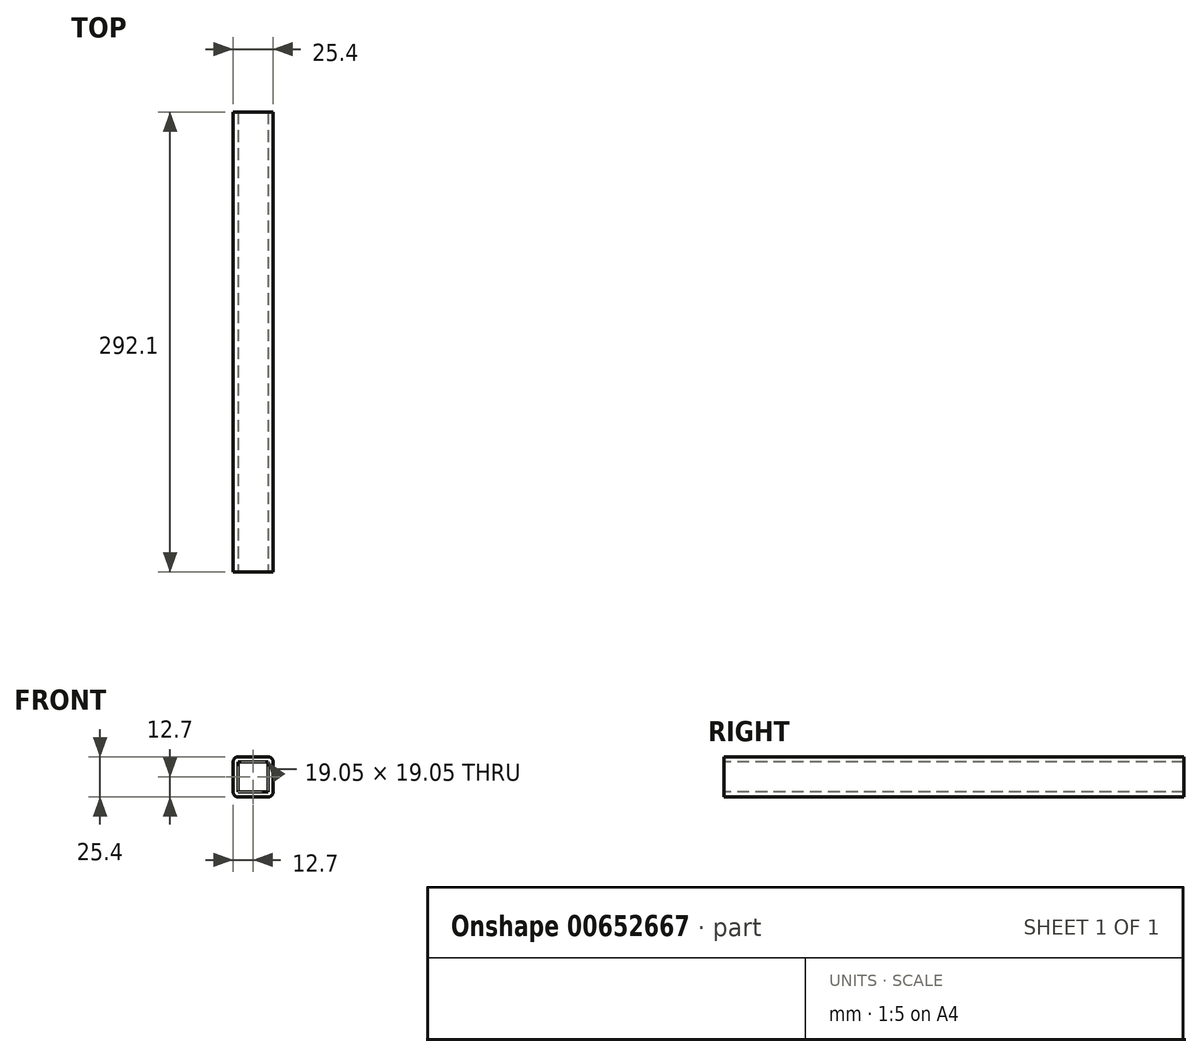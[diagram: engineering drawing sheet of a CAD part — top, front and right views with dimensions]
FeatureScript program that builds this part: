
annotation { "Feature Type Name" : "Feature", "Feature Type Description" : "" }
export const myFeature = defineFeature(function(context is Context, id is Id, definition is map)
    precondition{}
    {
        {
            var Q0;
            Q0=qCreatedBy(makeId("Front.planeOp"),FACE);
            var sketch = newSketch(context, id + "F0", { "sketchPlane" : qUnion([Q0])});
            skLineSegment(sketch, "E0.bottom", {"start": v(12.7, -12.7) * mm, "end": v(-12.7, -12.7) * mm});
            skLineSegment(sketch, "E0.top", {"start": v(12.7, 12.7) * mm, "end": v(-12.7, 12.7) * mm});
            skLineSegment(sketch, "E0.left", {"start": v(12.7, -12.7) * mm, "end": v(12.7, 12.7) * mm});
            skLineSegment(sketch, "E0.right", {"start": v(-12.7, -12.7) * mm, "end": v(-12.7, 12.7) * mm});
            skPoint(sketch, "E0.middle", {"position": v(0, 0) * mm});
            skSolve(sketch);
        }
        {
            var Q0;
            Q0=makeQuery(id+"F0.imprint","IMPRINT",FACE,{"disambiguationData":[TD([[makeQuery(id+"F0.imprint","IMPRINT",EDGE,{"derivedFrom":sQuery(id+"F0.wireOp",EDGE,"E0.bottom")}),-1.0]])]});
            extrude(context, id + "F1", {"entities" : qUnion([Q0]), "depth" : 292.1 * mm, "offsetDistance" : 25.4 * mm});
        }
        {
            var Q0;
            Q0=makeQuery(id+"F1.opExtrude","SWEPT_EDGE",EDGE,{"disambiguationData":[OSD([sQuery(id+"F0.wireOp",EDGE,"E0.top"),sQuery(id+"F0.wireOp",EDGE,"E0.right")])]});
            var Q1;
            Q1=makeQuery(id+"F1.opExtrude","SWEPT_EDGE",EDGE,{"disambiguationData":[OSD([sQuery(id+"F0.wireOp",EDGE,"E0.top"),sQuery(id+"F0.wireOp",EDGE,"E0.left")])]});
            var Q2;
            Q2=makeQuery(id+"F1.opExtrude","SWEPT_EDGE",EDGE,{"disambiguationData":[OSD([sQuery(id+"F0.wireOp",EDGE,"E0.bottom"),sQuery(id+"F0.wireOp",EDGE,"E0.left")])]});
            var Q3;
            Q3=makeQuery(id+"F1.opExtrude","SWEPT_EDGE",EDGE,{"disambiguationData":[OSD([sQuery(id+"F0.wireOp",EDGE,"E0.bottom"),sQuery(id+"F0.wireOp",EDGE,"E0.right")])]});
            fillet(context, id + "F2", {"entities" : qUnion([Q0, Q1, Q2, Q3]), "radius" : 3.17 * mm, "tangentPropagation" : true, "allowEdgeOverflow" : false});
        }
        {
            var Q0;
            Q0=makeQuery(id+"F1.opExtrude","CAP_FACE",FACE,{"disambiguationData":[OSD([sQuery(id+"F0.wireOp",EDGE,"E0.bottom"),sQuery(id+"F0.wireOp",EDGE,"E0.top"),sQuery(id+"F0.wireOp",EDGE,"E0.left"),sQuery(id+"F0.wireOp",EDGE,"E0.right")])],"isStart":false});
            var Q1;
            Q1=makeQuery(id+"F1.opExtrude","CAP_FACE",FACE,{"disambiguationData":[OSD([sQuery(id+"F0.wireOp",EDGE,"E0.bottom"),sQuery(id+"F0.wireOp",EDGE,"E0.top"),sQuery(id+"F0.wireOp",EDGE,"E0.left"),sQuery(id+"F0.wireOp",EDGE,"E0.right")])],"isStart":true});
            shell(context, id + "F3", {"entities" : qUnion([Q0, Q1]), "thickness" : 3.17 * mm});
        }
    });
